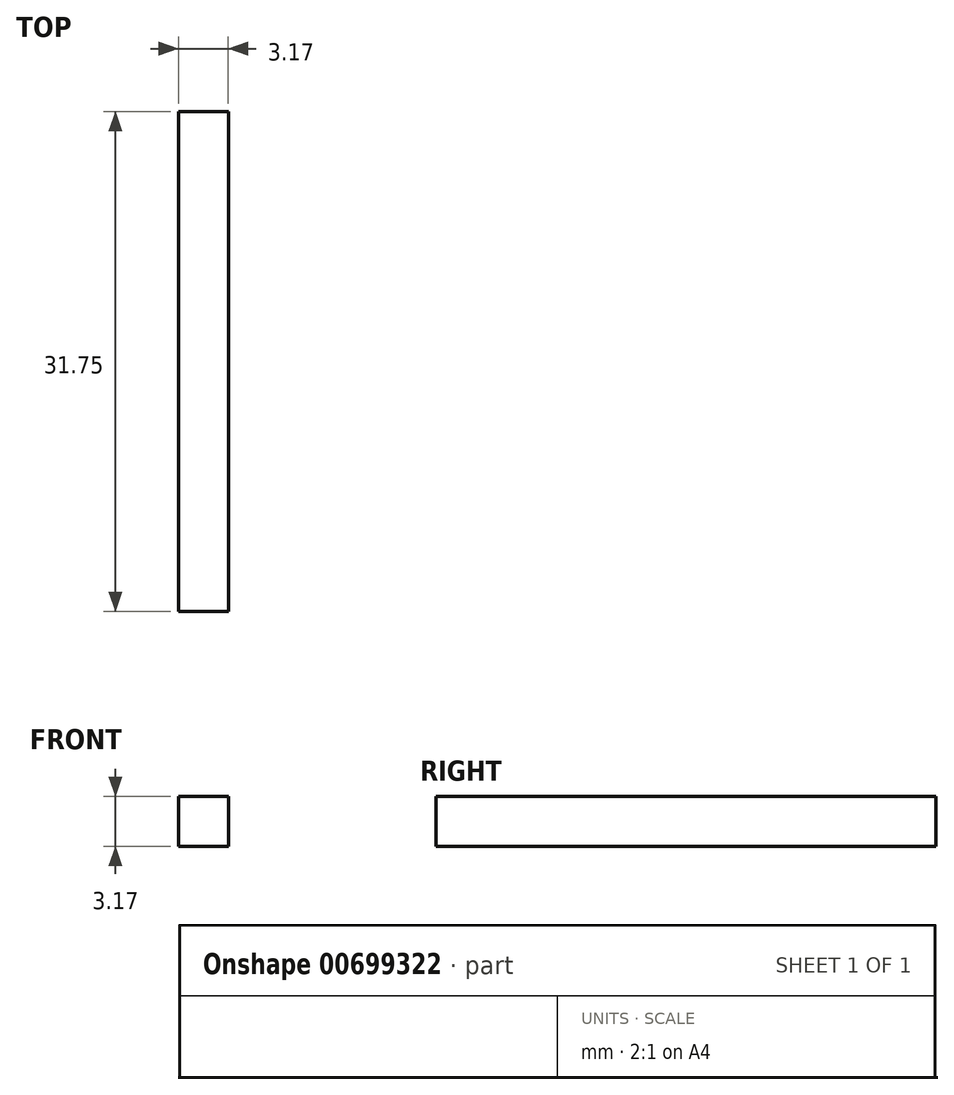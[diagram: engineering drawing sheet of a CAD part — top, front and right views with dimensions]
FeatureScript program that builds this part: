
annotation { "Feature Type Name" : "Feature", "Feature Type Description" : "" }
export const myFeature = defineFeature(function(context is Context, id is Id, definition is map)
    precondition{}
    {
        {
            var Q0;
            Q0=qCreatedBy(makeId("Front.planeOp"),FACE);
            var sketch = newSketch(context, id + "F0", { "sketchPlane" : qUnion([Q0])});
            skLineSegment(sketch, "E0.bottom", {"start": v(0, 0) * mm, "end": v(3.18, 0) * mm});
            skLineSegment(sketch, "E0.top", {"start": v(0, 3.18) * mm, "end": v(3.17, 3.18) * mm});
            skLineSegment(sketch, "E0.left", {"start": v(0, 0) * mm, "end": v(0, 3.18) * mm});
            skLineSegment(sketch, "E0.right", {"start": v(3.18, 0) * mm, "end": v(3.18, 3.18) * mm});
            skSolve(sketch);
        }
        {
            var Q0;
            Q0=makeQuery(id+"F0.imprint","IMPRINT",FACE,{"disambiguationData":[TD([[makeQuery(id+"F0.imprint","IMPRINT",EDGE,{"derivedFrom":sQuery(id+"F0.wireOp",EDGE,"E0.bottom")}),1.0]])]});
            extrude(context, id + "F1", {"entities" : qUnion([Q0]), "depth" : 31.75 * mm, "offsetDistance" : 25.4 * mm});
        }
    });
